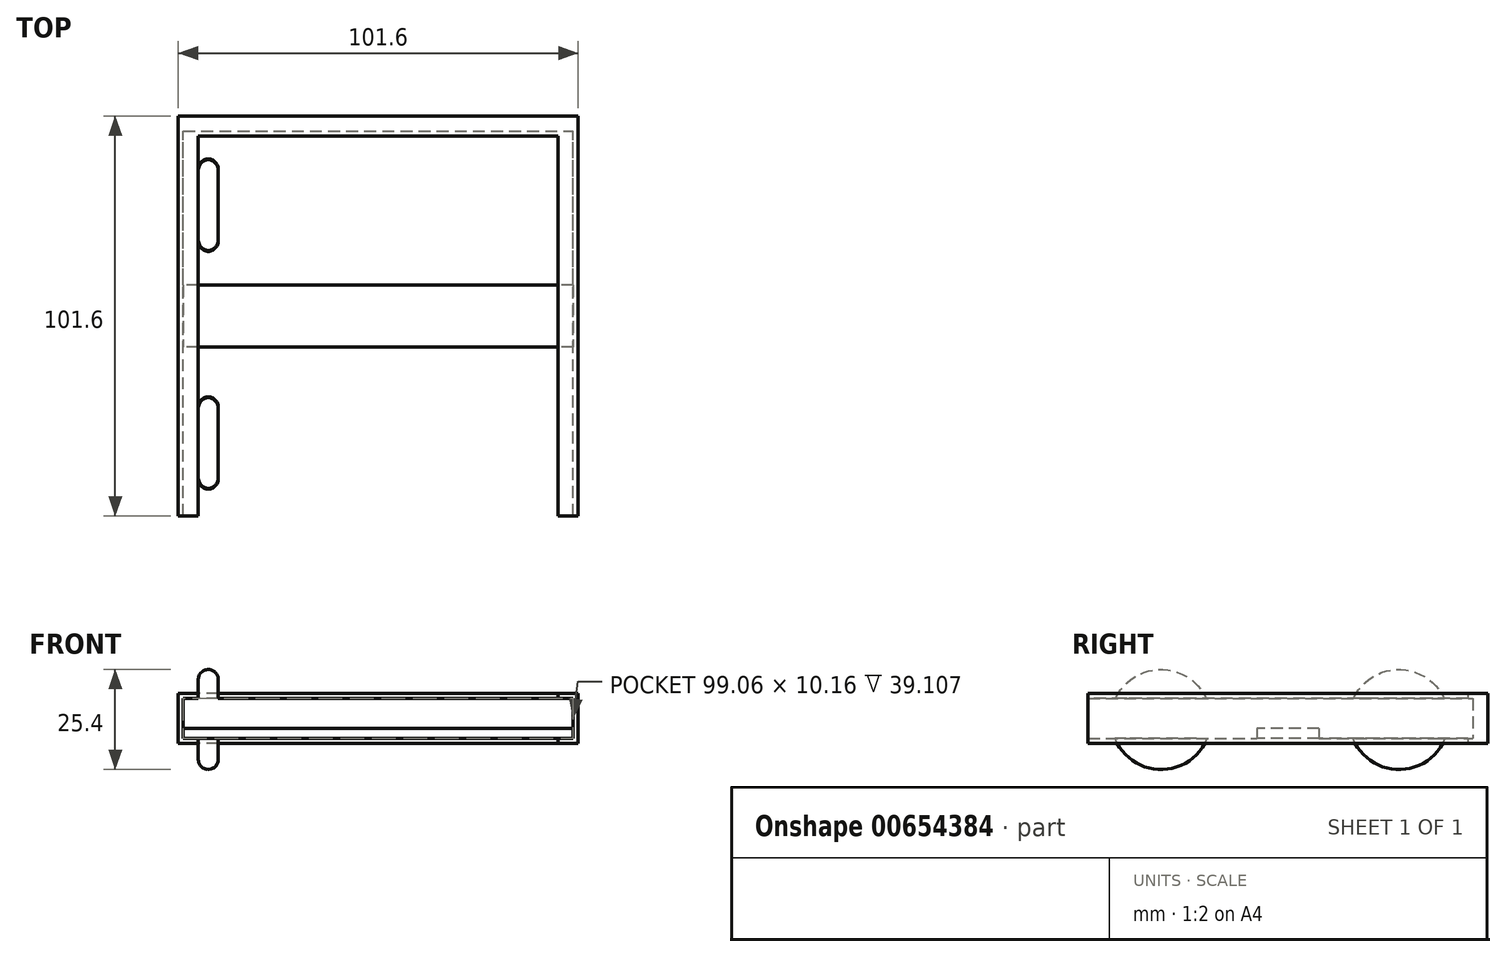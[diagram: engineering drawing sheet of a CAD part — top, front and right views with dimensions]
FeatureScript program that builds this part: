
annotation { "Feature Type Name" : "Feature", "Feature Type Description" : "" }
export const myFeature = defineFeature(function(context is Context, id is Id, definition is map)
    precondition{}
    {
        {
            var Q0;
            Q0=qCreatedBy(makeId("Top.planeOp"),FACE);
            var sketch = newSketch(context, id + "F0", { "sketchPlane" : qUnion([Q0])});
            skLineSegment(sketch, "E0.bottom", {"start": v(50.8, 50.8) * mm, "end": v(-50.8, 50.8) * mm});
            skLineSegment(sketch, "E0.top", {"start": v(50.8, -50.8) * mm, "end": v(45.72, -50.8) * mm});
            skLineSegment(sketch, "E0.left", {"start": v(50.8, 50.8) * mm, "end": v(50.8, -50.8) * mm});
            skLineSegment(sketch, "E0.right", {"start": v(-50.8, 50.8) * mm, "end": v(-50.8, -50.8) * mm});
            skPoint(sketch, "E0.middle", {"position": v(0, 0) * mm});
            skLineSegment(sketch, "E1.bottom", {"start": v(45.72, 45.72) * mm, "end": v(-45.72, 45.72) * mm});
            skLineSegment(sketch, "E1.left", {"start": v(45.72, 45.72) * mm, "end": v(45.72, -45.72) * mm});
            skLineSegment(sketch, "E1.right", {"start": v(-45.72, 45.72) * mm, "end": v(-45.72, -45.72) * mm});
            skLineSegment(sketch, "E2", {"start": v(-45.72, -45.72) * mm, "end": v(-45.72, -50.8) * mm});
            skLineSegment(sketch, "E3", {"start": v(45.72, -45.72) * mm, "end": v(45.72, -50.8) * mm});
            skLineSegment(sketch, "E4.trimOffspring", {"start": v(-45.72, -50.8) * mm, "end": v(-50.8, -50.8) * mm});
            skSolve(sketch);
        }
        {
            var Q0;
            Q0 = qSketchRegion(id + "F0", true);
            extrude(context, id + "F1", {"entities" : qUnion([Q0]), "depth" : 12.7 * mm, "offsetDistance" : 25.4 * mm});
        }
        {
            var Q0;
            Q0=makeQuery(id+"F1.opExtrude","SWEPT_FACE",FACE,{"disambiguationData":[OSD([sQuery(id+"F0.wireOp",EDGE,"E1.right"),sQuery(id+"F0.wireOp",EDGE,"E2")])]});
            cPlane(context, id + "F2", {"entities" : qUnion([Q0]), "cplaneType" : CPlaneType.OFFSET, "offset" : 0 * mm, "width" : 152.4 * mm, "height" : 152.4 * mm});
        }
        {
            var Q0;
            Q0=qCreatedBy(id+"F2.planeOp",FACE);
            var sketch = newSketch(context, id + "F3", { "sketchPlane" : qUnion([Q0])});
            skCircle(sketch, "E5", {"center": v(-32.26, 6.1) * mm, "radius": 12.7 * mm});
            skCircle(sketch, "E6", {"center": v(28.18, 6.1) * mm, "radius": 12.7 * mm});
            skSolve(sketch);
        }
        {
            var Q0;
            Q0 = qSketchRegion(id + "F3", true);
            extrude(context, id + "F4", {"entities" : qUnion([Q0]), "depth" : 5.08 * mm, "offsetDistance" : 25.4 * mm});
        }
        {
            var Q0;
            Q0=makeQuery(id+"F4.opExtrude","CAP_EDGE",EDGE,{"disambiguationData":[OSD([sQuery(id+"F3.wireOp",EDGE,"E5")])],"isStart":false});
            var Q1;
            Q1=makeQuery(id+"F4.opExtrude","CAP_EDGE",EDGE,{"disambiguationData":[OSD([sQuery(id+"F3.wireOp",EDGE,"E5")])],"isStart":true});
            var Q2;
            Q2=makeQuery(id+"F4.opExtrude","CAP_EDGE",EDGE,{"disambiguationData":[OSD([sQuery(id+"F3.wireOp",EDGE,"E6")])],"isStart":true});
            var Q3;
            Q3=makeQuery(id+"F4.opExtrude","CAP_EDGE",EDGE,{"disambiguationData":[OSD([sQuery(id+"F3.wireOp",EDGE,"E6")])],"isStart":false});
            fillet(context, id + "F5", {"entities" : qUnion([Q0, Q1, Q2, Q3]), "radius" : 2.54 * mm, "tangentPropagation" : true, "allowEdgeOverflow" : false});
        }
        {
            var Q0;
            Q0=qCreatedBy(makeId("Top.planeOp"),FACE);
            cPlane(context, id + "F6", {"entities" : qUnion([Q0]), "cplaneType" : CPlaneType.OFFSET, "offset" : 1.27 * mm, "width" : 152.4 * mm, "height" : 152.4 * mm});
        }
        {
            var Q0;
            Q0=qCreatedBy(id+"F6.planeOp",FACE);
            var sketch = newSketch(context, id + "F7", { "sketchPlane" : qUnion([Q0])});
            skLineSegment(sketch, "E7.top", {"start": v(-49.53, 47) * mm, "end": v(49.53, 47) * mm});
            skLineSegment(sketch, "E7.left", {"start": v(-49.53, -47) * mm, "end": v(-49.53, 47) * mm});
            skLineSegment(sketch, "E7.right", {"start": v(49.53, -47) * mm, "end": v(49.53, 47) * mm});
            skPoint(sketch, "E7.middle", {"position": v(0, 0) * mm});
            skLineSegment(sketch, "E8", {"start": v(-49.53, -47) * mm, "end": v(-49.53, -61.86) * mm});
            skLineSegment(sketch, "E9.bottom", {"start": v(-49.53, -61.86) * mm, "end": v(49.53, -61.86) * mm});
            skLineSegment(sketch, "E9.left", {"start": v(-49.53, -61.86) * mm, "end": v(-49.53, -47) * mm});
            skLineSegment(sketch, "E9.right", {"start": v(49.53, -61.86) * mm, "end": v(49.53, -47) * mm});
            skSolve(sketch);
        }
        {
            var Q0;
            Q0 = qSketchRegion(id + "F7", true);
            extrude(context, id + "F8", {"entities" : qUnion([Q0]), "operationType" : NewBodyOperationType.REMOVE, "depth" : 10.16 * mm, "offsetDistance" : 25.4 * mm});
        }
        {
            var Q0;
            Q0=qCreatedBy(id+"F6.planeOp",FACE);
            var sketch = newSketch(context, id + "F9", { "sketchPlane" : qUnion([Q0])});
            skLineSegment(sketch, "E10.bottom", {"start": v(49.53, 7.88) * mm, "end": v(-49.53, 7.88) * mm});
            skLineSegment(sketch, "E10.top", {"start": v(49.53, -7.88) * mm, "end": v(-49.53, -7.88) * mm});
            skLineSegment(sketch, "E10.left", {"start": v(49.53, 7.88) * mm, "end": v(49.53, -7.88) * mm});
            skLineSegment(sketch, "E10.right", {"start": v(-49.53, 7.88) * mm, "end": v(-49.53, -7.88) * mm});
            skPoint(sketch, "E10.middle", {"position": v(0, 0) * mm});
            skSolve(sketch);
        }
        {
            var Q0;
            Q0 = qSketchRegion(id + "F9", true);
            extrude(context, id + "F10", {"entities" : qUnion([Q0]), "operationType" : NewBodyOperationType.ADD, "depth" : 2.54 * mm, "offsetDistance" : 25.4 * mm});
        }
    });
